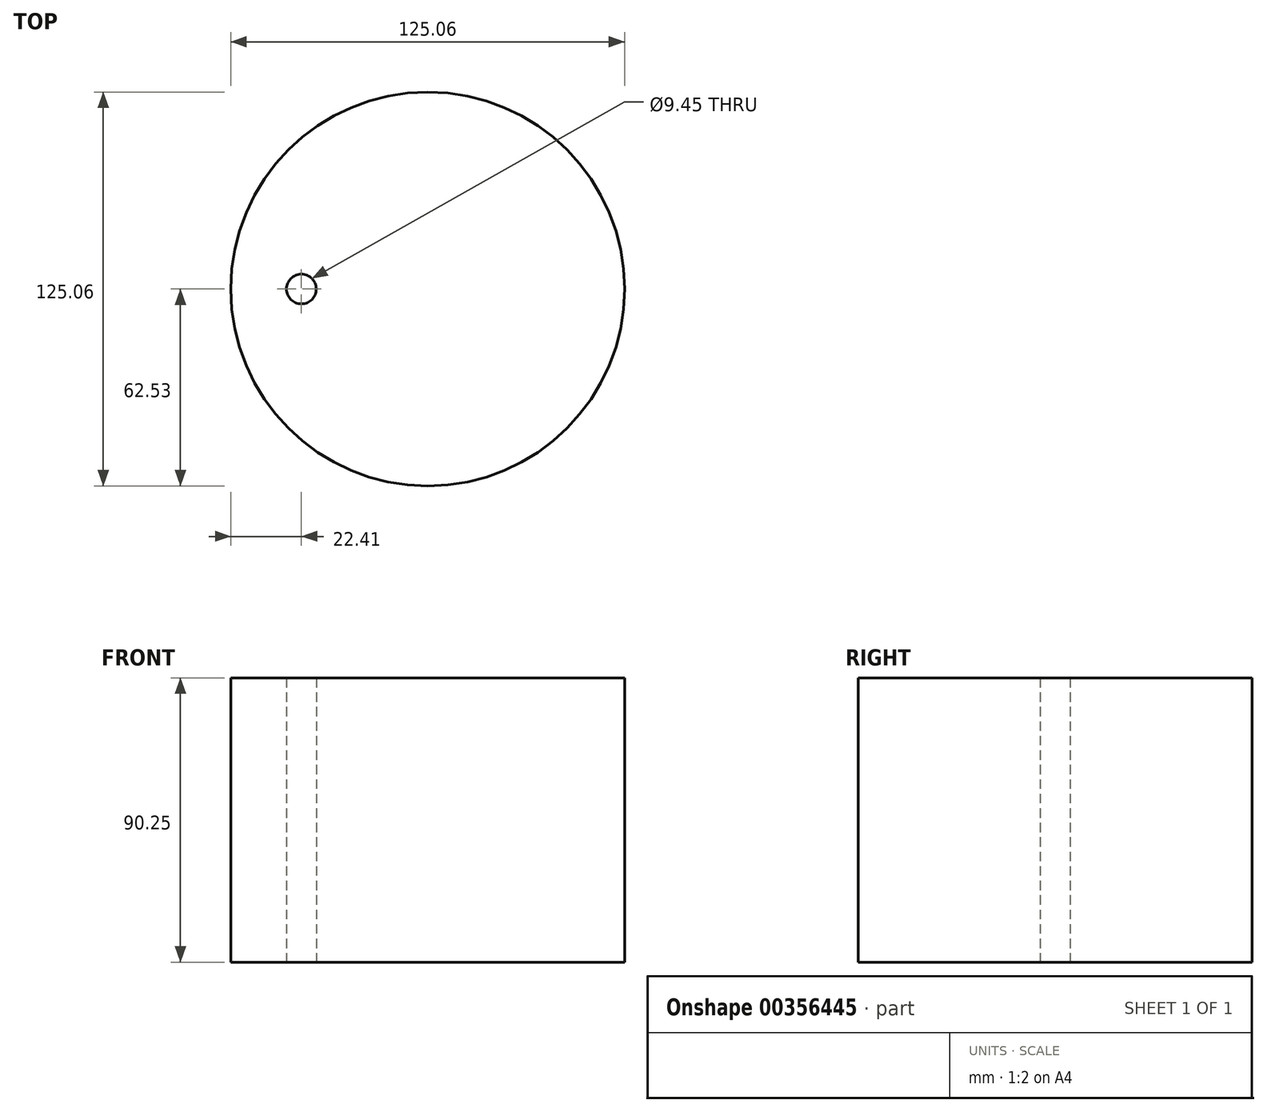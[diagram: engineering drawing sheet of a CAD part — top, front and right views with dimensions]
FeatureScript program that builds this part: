
annotation { "Feature Type Name" : "Feature", "Feature Type Description" : "" }
export const myFeature = defineFeature(function(context is Context, id is Id, definition is map)
    precondition{}
    {
        {
            var Q0;
            Q0=qCreatedBy(makeId("Top.planeOp"),FACE);
            var sketch = newSketch(context, id + "F0", { "sketchPlane" : qUnion([Q0])});
            skCircle(sketch, "E0", {"center": v(0, 0) * mm, "radius": 4.72 * mm});
            skCircle(sketch, "E1", {"center": v(40.12, 0) * mm, "radius": 62.53 * mm});
            skSolve(sketch);
        }
        {
            var Q0;
            Q0=makeQuery(id+"F0.imprint","IMPRINT",FACE,{"disambiguationData":[TD([[makeQuery(id+"F0.imprint","IMPRINT",EDGE,{"derivedFrom":sQuery(id+"F0.wireOp",EDGE,"E0")}),-1.0]])]});
            extrude(context, id + "F1", {"entities" : qUnion([Q0]), "depth" : 90.25 * mm});
        }
    });
